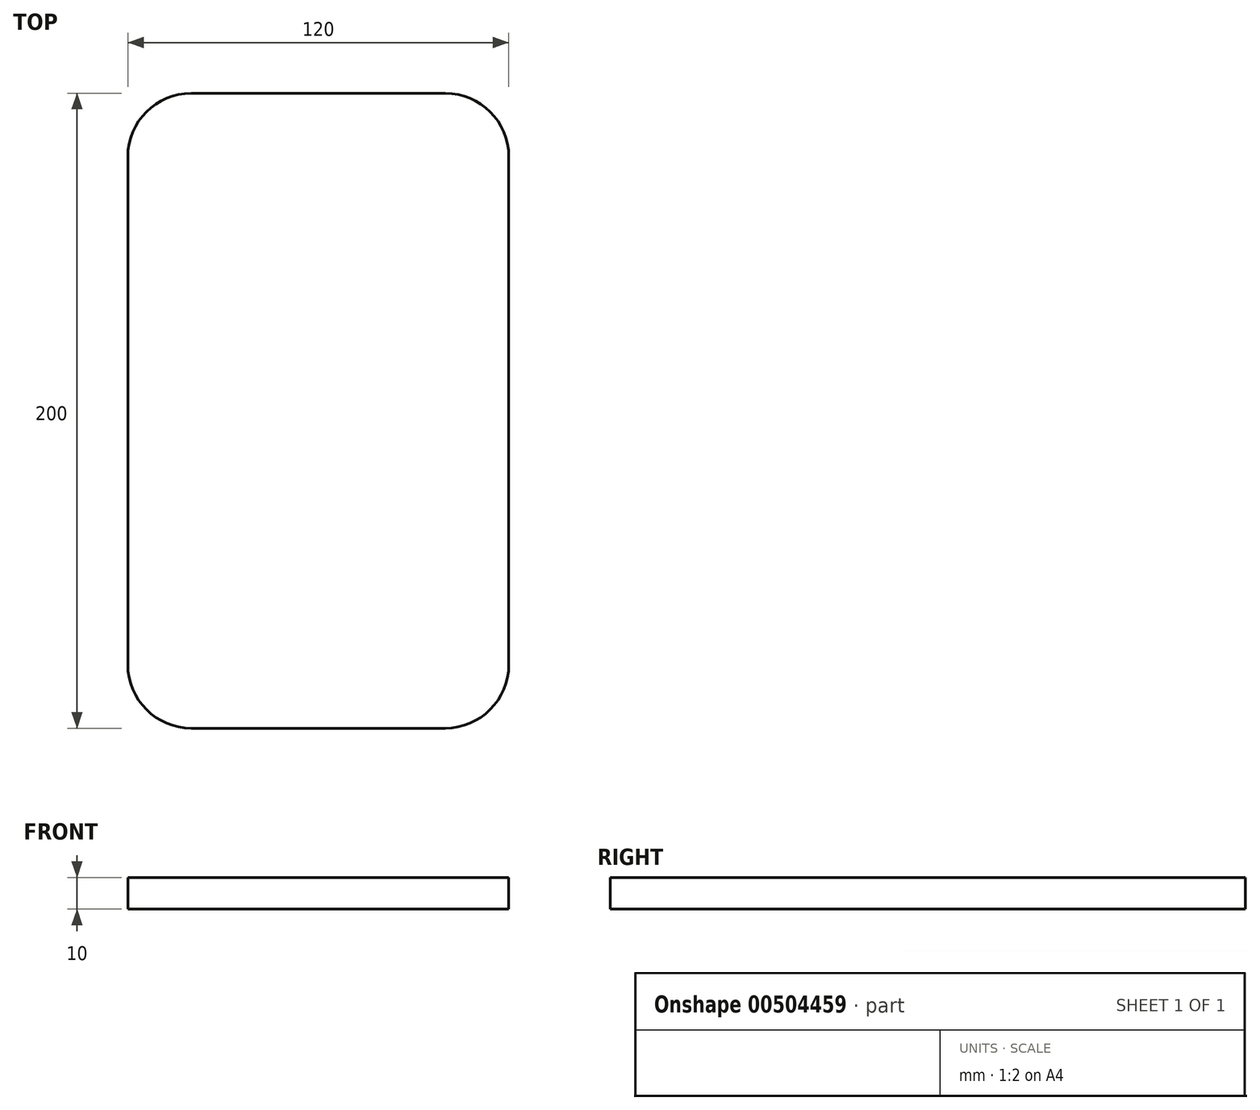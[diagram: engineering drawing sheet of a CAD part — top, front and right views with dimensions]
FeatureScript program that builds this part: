
annotation { "Feature Type Name" : "Feature", "Feature Type Description" : "" }
export const myFeature = defineFeature(function(context is Context, id is Id, definition is map)
    precondition{}
    {
        {
            var Q0;
            Q0=qCreatedBy(makeId("Top.planeOp"),FACE);
            var sketch = newSketch(context, id + "F0", { "sketchPlane" : qUnion([Q0])});
            skLineSegment(sketch, "E0.bottom", {"start": v(-40, 100) * mm, "end": v(40, 100) * mm});
            skLineSegment(sketch, "E0.top", {"start": v(-40, -100) * mm, "end": v(40, -100) * mm});
            skLineSegment(sketch, "E0.left", {"start": v(-60, 80) * mm, "end": v(-60, -80) * mm});
            skLineSegment(sketch, "E0.right", {"start": v(60, 80) * mm, "end": v(60, -80) * mm});
            skPoint(sketch, "E0.middle", {"position": v(0, 0) * mm});
            skPoint(sketch, "E1.visualSharp", {"position": v(60, -100) * mm});
            skArc(sketch, "E1.filletArc", {"start": v(40, -100) * mm, "mid": v(54.14, -94.14) * mm, "end": v(60, -80) * mm});
            skPoint(sketch, "E2.visualSharp", {"position": v(60, 100) * mm});
            skArc(sketch, "E2.filletArc", {"start": v(60, 80) * mm, "mid": v(54.14, 94.14) * mm, "end": v(40, 100) * mm});
            skPoint(sketch, "E3.visualSharp", {"position": v(-60, -100) * mm});
            skArc(sketch, "E3.filletArc", {"start": v(-60, -80) * mm, "mid": v(-54.14, -94.14) * mm, "end": v(-40, -100) * mm});
            skPoint(sketch, "E4.visualSharp", {"position": v(-60, 100) * mm});
            skArc(sketch, "E4.filletArc", {"start": v(-40, 100) * mm, "mid": v(-54.14, 94.14) * mm, "end": v(-60, 80) * mm});
            skSolve(sketch);
        }
        {
            var Q0;
            Q0 = qSketchRegion(id + "F0", true);
            extrude(context, id + "F1", {"entities" : qUnion([Q0]), "depth" : 10 * mm});
        }
    });
